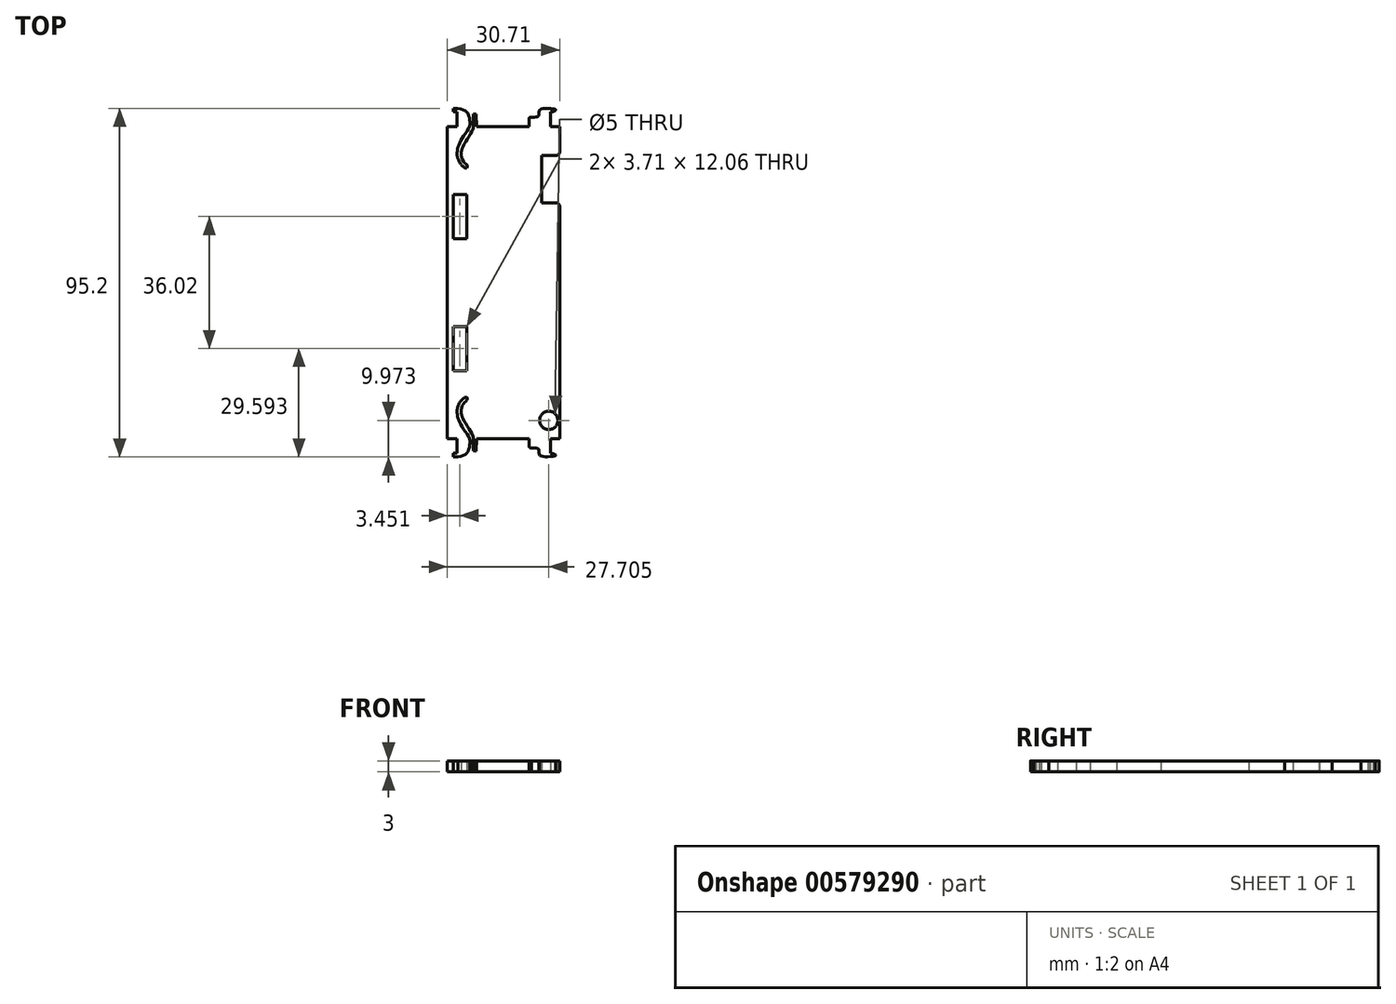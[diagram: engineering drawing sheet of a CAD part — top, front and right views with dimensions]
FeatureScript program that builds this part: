
annotation { "Feature Type Name" : "Feature", "Feature Type Description" : "" }
export const myFeature = defineFeature(function(context is Context, id is Id, definition is map)
    precondition{}
    {
        {
            var Q0;
            Q0=qCreatedBy(makeId("Top.planeOp"),FACE);
            var sketch = newSketch(context, id + "F0", { "sketchPlane" : qUnion([Q0])});
            skLineSegment(sketch, "E0.bottom", {"start": v(-12.9, 44.83) * mm, "end": v(-10.2, 44.83) * mm});
            skLineSegment(sketch, "E0.top", {"start": v(-12.9, -40.43) * mm, "end": v(-10.2, -40.43) * mm});
            skLineSegment(sketch, "E0.left", {"start": v(-12.9, 44.83) * mm, "end": v(-12.9, -40.43) * mm});
            skLineSegment(sketch, "E0.right", {"start": v(17.82, 44.83) * mm, "end": v(17.82, 37.9) * mm});
            skLineSegment(sketch, "E1.bottom", {"start": v(-11.3, 14.18) * mm, "end": v(-7.58, 14.18) * mm});
            skLineSegment(sketch, "E1.top", {"start": v(-11.3, 26.24) * mm, "end": v(-7.58, 26.24) * mm});
            skLineSegment(sketch, "E1.left", {"start": v(-11.3, 14.18) * mm, "end": v(-11.3, 26.24) * mm});
            skLineSegment(sketch, "E1.right", {"start": v(-7.58, 14.18) * mm, "end": v(-7.58, 26.24) * mm});
            skLineSegment(sketch, "E2.top", {"start": v(-11.2, 48.8) * mm, "end": v(-10.2, 48.8) * mm});
            skLineSegment(sketch, "E2.right", {"start": v(-10.2, 44.83) * mm, "end": v(-10.2, 48.8) * mm});
            skLineSegment(sketch, "E3", {"start": v(-11.2, 48.8) * mm, "end": v(-11.2, 49.8) * mm});
            skLineSegment(sketch, "E4", {"start": v(-11.2, 49.8) * mm, "end": v(-9.92, 49.8) * mm});
            skLineSegment(sketch, "E5", {"start": v(-10.2, 37.72) * mm, "end": v(-10.2, 37.02) * mm});
            skFitSpline(sketch, "E6", {"points": [v(-9.92, 49.8) * mm, v(-7.54, 48.75) * mm, v(-6.8, 46.82) * mm, v(-6.8, 44.83) * mm, v(-8.82, 41.68) * mm, v(-9.92, 39.23) * mm, v(-10.2, 37.72) * mm, v(-10.07, 36.27) * mm, v(-8.88, 34.2) * mm, v(-7.62, 33.53) * mm, v(-7.62, 33.87) * mm], "startDerivative": vector(24.68, -6.57) * mm, "endDerivative": vector(-9.27, 3.27) * mm});
            skFitSpline(sketch, "E7", {"points": [v(-7.62, 33.53) * mm, v(-7.4, 33.77) * mm, v(-7.56, 34.36) * mm, v(-8.22, 34.95) * mm, v(-9.03, 36.54) * mm, v(-9.1, 37.67) * mm, v(-8.83, 38.87) * mm, v(-7.49, 41.33) * mm, v(-6, 43.92) * mm, v(-5.76, 44.83) * mm], "startDerivative": vector(4.94, 3.3) * mm, "endDerivative": vector(1.2, 8.54) * mm});
            skLineSegment(sketch, "E8.trimOffspring", {"start": v(-4.96, 44.83) * mm, "end": v(9.43, 44.83) * mm});
            skPoint(sketch, "E9.orphan", {"position": v(-10.2, 33.53) * mm});
            skPoint(sketch, "E10.trimOffspring.end.orphan", {"position": v(-5.03, 33.53) * mm});
            skLineSegment(sketch, "E11", {"start": v(-5.76, 44.83) * mm, "end": v(-5.8, 48.2) * mm});
            skLineSegment(sketch, "E12", {"start": v(-5.8, 48.2) * mm, "end": v(-5, 48.2) * mm});
            skLineSegment(sketch, "E13", {"start": v(-5, 48.2) * mm, "end": v(-4.96, 44.83) * mm});
            skPoint(sketch, "E14.start.orphan", {"position": v(-10.2, 46.82) * mm});
            skPoint(sketch, "E15.end.orphan", {"position": v(-5, 46.82) * mm});
            skLineSegment(sketch, "E16.right", {"start": v(15.28, 44.83) * mm, "end": v(15.28, 48.8) * mm});
            skLineSegment(sketch, "E17.top", {"start": v(10.12, 47.4) * mm, "end": v(10.9, 47.4) * mm});
            skLineSegment(sketch, "E17.left", {"start": v(9.43, 44.83) * mm, "end": v(9.43, 46.76) * mm});
            skFitSpline(sketch, "E18", {"points": [v(15.28, 48.8) * mm, v(16.05, 48.94) * mm, v(16.65, 49.21) * mm, v(16.69, 49.43) * mm, v(16.12, 49.62) * mm, v(12.75, 49.59) * mm, v(12.17, 48.8) * mm, v(12.08, 47.7) * mm, v(10.9, 47.4) * mm, v(9.6, 47.27) * mm, v(9.43, 46.76) * mm], "startDerivative": vector(8.69, 1.47) * mm, "endDerivative": vector(-0.61, -8.23) * mm});
            skPoint(sketch, "E17.right.end.orphan", {"position": v(12.38, 47.4) * mm});
            skLineSegment(sketch, "E19.trimOffspring", {"start": v(15.28, 44.83) * mm, "end": v(17.82, 44.83) * mm});
            skPoint(sketch, "E20.orphan", {"position": v(9.43, 47.4) * mm});
            skLineSegment(sketch, "E21.MirrorCS", {"start": v(-11.2, -45.4) * mm, "end": v(-9.92, -45.4) * mm});
            skLineSegment(sketch, "E22.MirrorCS", {"start": v(-11.2, -44.4) * mm, "end": v(-10.2, -44.4) * mm});
            skLineSegment(sketch, "E23.MirrorCS", {"start": v(-11.2, -44.4) * mm, "end": v(-11.2, -45.4) * mm});
            skLineSegment(sketch, "E24.MirrorCS", {"start": v(-5.8, -43.8) * mm, "end": v(-5, -43.8) * mm});
            skLineSegment(sketch, "E25.MirrorCS", {"start": v(10.12, -42.98) * mm, "end": v(10.9, -42.98) * mm});
            skLineSegment(sketch, "E26.MirrorCS", {"start": v(15.28, -40.43) * mm, "end": v(17.82, -40.43) * mm});
            skLineSegment(sketch, "E27.MirrorCS", {"start": v(-10.2, -40.43) * mm, "end": v(-10.2, -44.4) * mm});
            skLineSegment(sketch, "E28.MirrorCS", {"start": v(-10.2, -33.31) * mm, "end": v(-10.2, -32.61) * mm});
            skLineSegment(sketch, "E29.MirrorCS", {"start": v(9.43, -40.43) * mm, "end": v(9.43, -42.36) * mm});
            skFitSpline(sketch, "E30.MirrorCS", {"points": [v(-7.62, -29.13) * mm, v(-7.4, -29.36) * mm, v(-7.56, -29.96) * mm, v(-8.22, -30.54) * mm, v(-9.03, -32.13) * mm, v(-9.1, -33.26) * mm, v(-8.83, -34.46) * mm, v(-7.49, -36.93) * mm, v(-6, -39.5) * mm, v(-5.76, -40.43) * mm], "startDerivative": vector(4.94, -3.3) * mm, "endDerivative": vector(1.2, -8.54) * mm});
            skPoint(sketch, "E31.MirrorP", {"position": v(-10.2, -42.41) * mm});
            skLineSegment(sketch, "E32.MirrorCS", {"start": v(-5, -43.8) * mm, "end": v(-4.96, -40.43) * mm});
            skLineSegment(sketch, "E33.MirrorCS", {"start": v(-5.76, -40.43) * mm, "end": v(-5.8, -43.8) * mm});
            skLineSegment(sketch, "E34.MirrorCS", {"start": v(-11.3, -21.84) * mm, "end": v(-7.58, -21.84) * mm});
            skFitSpline(sketch, "E35.MirrorCS", {"points": [v(15.28, -44.39) * mm, v(16.05, -44.53) * mm, v(16.65, -44.8) * mm, v(16.69, -45.02) * mm, v(16.12, -45.22) * mm, v(12.75, -45.18) * mm, v(12.17, -44.39) * mm, v(12.08, -43.3) * mm, v(10.9, -42.98) * mm, v(9.6, -42.86) * mm, v(9.43, -42.36) * mm], "startDerivative": vector(8.69, -1.47) * mm, "endDerivative": vector(-0.61, 8.23) * mm});
            skPoint(sketch, "E36.MirrorP", {"position": v(9.43, -42.98) * mm});
            skPoint(sketch, "E37.MirrorP", {"position": v(-10.2, -29.13) * mm});
            skLineSegment(sketch, "E38.MirrorCS", {"start": v(-11.3, -9.78) * mm, "end": v(-11.3, -21.84) * mm});
            skPoint(sketch, "E39.MirrorP", {"position": v(12.38, -42.98) * mm});
            skLineSegment(sketch, "E40.MirrorCS", {"start": v(-7.58, -9.78) * mm, "end": v(-7.58, -21.84) * mm});
            skFitSpline(sketch, "E41.MirrorCS", {"points": [v(-9.92, -45.4) * mm, v(-7.54, -44.34) * mm, v(-6.8, -42.41) * mm, v(-6.8, -40.43) * mm, v(-8.82, -37.27) * mm, v(-9.92, -34.83) * mm, v(-10.2, -33.31) * mm, v(-10.07, -31.87) * mm, v(-8.88, -29.79) * mm, v(-7.62, -29.13) * mm, v(-7.62, -29.46) * mm], "startDerivative": vector(24.68, 6.57) * mm, "endDerivative": vector(-9.27, -3.27) * mm});
            skLineSegment(sketch, "E42.MirrorCS", {"start": v(-4.96, -40.43) * mm, "end": v(9.43, -40.43) * mm});
            skPoint(sketch, "E43.MirrorP", {"position": v(-5, -42.41) * mm});
            skLineSegment(sketch, "E44.MirrorCS", {"start": v(-11.3, -9.78) * mm, "end": v(-7.58, -9.78) * mm});
            skLineSegment(sketch, "E45.MirrorCS", {"start": v(15.28, -40.43) * mm, "end": v(15.28, -44.39) * mm});
            skPoint(sketch, "E46.MirrorP", {"position": v(-5.03, -29.13) * mm});
            skPoint(sketch, "E47.end.orphan", {"position": v(-12.9, 2.2) * mm});
            skPoint(sketch, "E47.start.orphan", {"position": v(17.82, 2.2) * mm});
            skLineSegment(sketch, "E48.bottom", {"start": v(12.89, 23.95) * mm, "end": v(16.82, 23.95) * mm});
            skLineSegment(sketch, "E48.top", {"start": v(12.89, 36.9) * mm, "end": v(16.82, 36.9) * mm});
            skLineSegment(sketch, "E48.left", {"start": v(12.89, 23.95) * mm, "end": v(12.89, 36.9) * mm});
            skLineSegment(sketch, "E49", {"start": v(17.82, 36.9) * mm, "end": v(16.82, 36.9) * mm});
            skArc(sketch, "E50", {"start": v(17.82, 22.95) * mm, "mid": v(17.52, 23.66) * mm, "end": v(16.82, 23.95) * mm});
            skArc(sketch, "E51", {"start": v(16.82, 36.9) * mm, "mid": v(17.52, 37.2) * mm, "end": v(17.82, 37.9) * mm});
            skLineSegment(sketch, "E52.trimOffspring", {"start": v(17.82, 22.95) * mm, "end": v(17.82, -40.43) * mm});
            skPoint(sketch, "E53.orphan", {"position": v(17.82, 23.95) * mm});
            skCircle(sketch, "E54", {"center": v(14.82, -35.43) * mm, "radius": 2.5 * mm});
            skSolve(sketch);
        }
        {
            var Q0;
            Q0=makeQuery(id+"F0.imprint","IMPRINT",FACE,{"disambiguationData":[TD([[makeQuery(id+"F0.imprint","IMPRINT",EDGE,{"derivedFrom":sQuery(id+"F0.wireOp",EDGE,"E0.left")}),1.0]])]});
            extrude(context, id + "F1", {"entities" : qUnion([Q0]), "depth" : 3 * mm, "offsetDistance" : 25.4 * mm});
        }
    });
